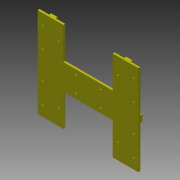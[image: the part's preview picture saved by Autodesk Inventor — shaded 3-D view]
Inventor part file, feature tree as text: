
AUTODESK INVENTOR PART (.ipt)
format: ipt  version: 2015 (Build 190159000, 159)  size: 469,504 bytes
history: native  units: mm
features: extrude x15, sketch x10, fillet x8, other x1, revolve x1
ambient origin geometry x8: Origin, YZ Plane, XZ Plane, XY Plane, X Axis, Y Axis, Z Axis, Center Point
bodies: Body1 (feature_tree)
feature tree (35):
  other  "Sólido1"
  sketch  "Boceto1"  dims[d0=37.0mm d1=57.0mm]
  extrude  "Extrusión1"  Depth=57.0mm
  extrude  "Extrusión2"  Depth=10.0mm
  extrude  "Extrusión3"  Depth=57.0mm
  sketch  "Boceto3"  dims[d4=20.0mm d5=57.0mm]
  extrude  "Extrusión4"  Depth=79.0mm
  extrude  "Extrusión5"  Depth=36.0mm
  extrude  "Extrusión6"  Depth=72.0mm
  extrude  "Extrusión7"  Depth=40.0mm
  fillet  "Empalme2"  Radius=3.0mm
  fillet  "Empalme3"  Radius=40.0mm
  fillet  "Empalme4"  Radius=13.0mm
  fillet  "Empalme5"  Radius=1111.0mm
  extrude  "Extrusión10"  Depth=5.0mm TaperAngle=0.0deg
  fillet  "Empalme10"  Radius=111.0mm
  sketch  "Boceto6"  dims[d6=37.0mm d7=79.0mm]
  extrude  "Extrusión11"  Depth=3.0mm
  extrude  "Extrusión12"  Depth=10.0mm
  fillet  "Empalme11"  Radius=2.0mm
  fillet  "Empalme12"  Radius=3.0mm
  revolve  "Revolución1"  [1 undecoded]
  fillet  "Empalme13"  Radius=2.5mm
  extrude  "Extrusión14"  Depth=10.0mm
  extrude  "Extrusión15"  Depth=3.0mm TaperAngle=0.0deg
  extrude  "Extrusión16"  Depth=3.0mm TaperAngle=0.0deg
  extrude  "Extrusión17"  Depth=10.0mm
  extrude  "Extrusión18"  Depth=10.0mm
  sketch  "Boceto2"  dims[d2=20.0mm d3=10.0mm]
  sketch  "Boceto8"  dims[d8=6.0mm d9=36.0mm]
  sketch  "Boceto9"  dims[d10=7.0mm d11=72.0mm]
  sketch  "Boceto10"  dims[d16=290.0mm d17=5.0mm d18=3.0mm d19=0.0mm d20=40.0mm d21=0.0mm d22=13.0mm d23=1111.0mm d24=0.0mm]
  sketch  "Boceto11"  dims[d25=5.0mm d26=0.0mm d27=5.0mm d28=0.0mm d29=111.0mm d30=0.0mm]
  sketch  "Boceto12"  dims[d31=3.0mm d32=0.0mm d41=1.0mm]
  sketch  "Boceto13"  dims[d42=5.0mm d43=5.0mm d44=2.0mm d47=3.0mm d48=0.0mm d51=1.0mm d53=2.5mm d54=6.5mm d55=3.0mm d56=0.0mm d57=3.0mm d58=0.0mm d59=1.0mm d60=2.0mm d63=19.5mm d64=19.5mm d65=180.0deg d66=10.0mm d67=270.0mm d68=10.0mm d69=0.0mm d70=292.0mm d71=300.0mm d72=270.0mm d73=10.0mm d74=6.0mm d75=3.0mm d76=0.5mm d77=35.0mm d78=3.0mm d79=0.5mm d80=6.0mm d81=35.0mm d82=40.0mm d84=360.0deg d86=8.0mm d87=0.0mm d88=20.0mm d89=75.0mm d90=40.0mm d91=140.0mm d95=50.0mm d96=40.0mm d97=107.0mm d98=2222.0mm d99=0.0mm d100=5.0mm d101=10.0mm d102=5.0mm d103=10.0mm d104=5.0mm d105=10.0mm d106=3.2mm d107=0.0mm d108=3.0mm d109=3.0mm d110=3.0mm d111=3.0mm d112=10.0mm d113=0.0mm]
note: 1 required parameter value undecoded (feature->parameter linkage not recoverable at this tier; creation-order binding heuristic only, values carry confidence <= 0.55)
